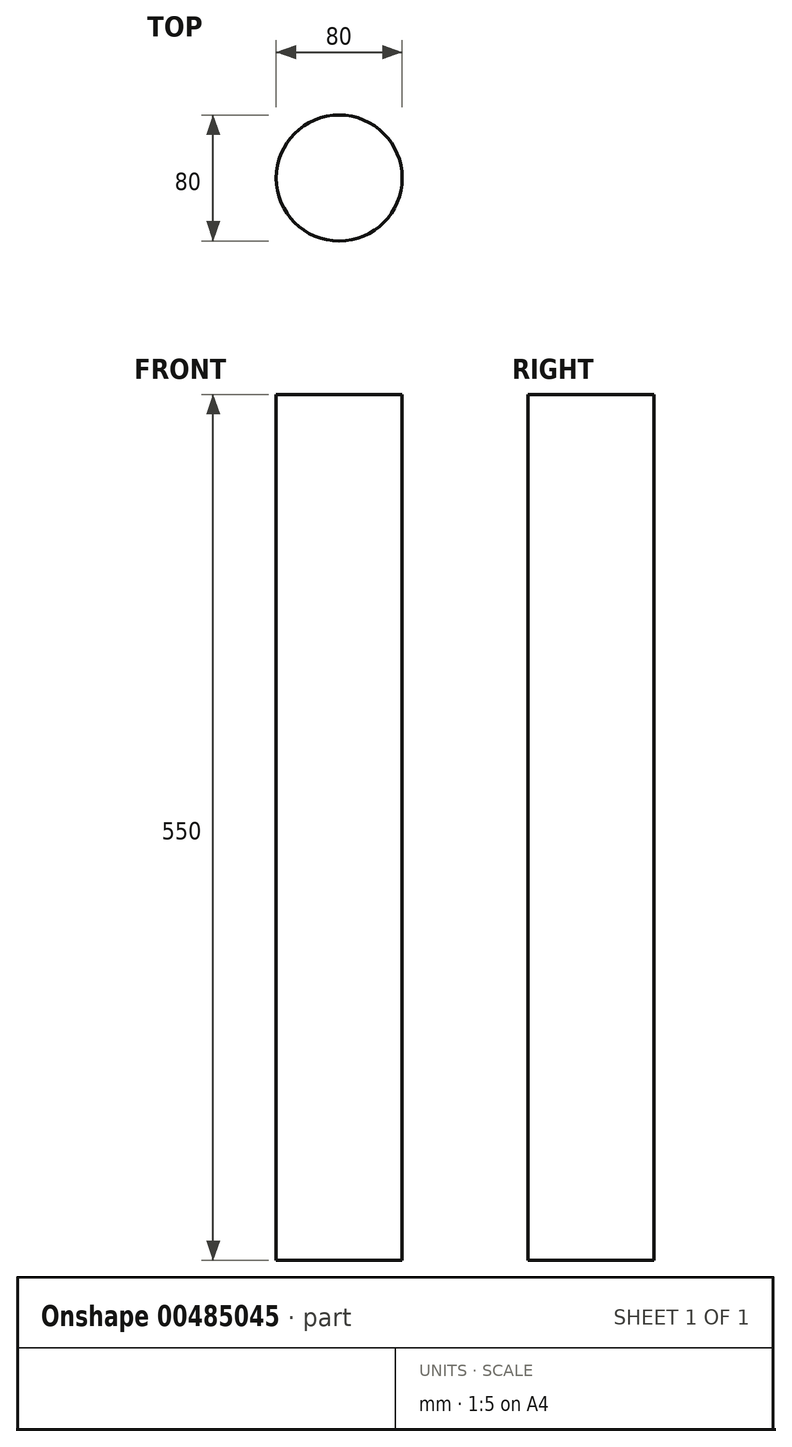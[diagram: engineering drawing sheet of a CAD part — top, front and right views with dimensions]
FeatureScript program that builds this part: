
annotation { "Feature Type Name" : "Feature", "Feature Type Description" : "" }
export const myFeature = defineFeature(function(context is Context, id is Id, definition is map)
    precondition{}
    {
        {
            var Q0;
            Q0=qCreatedBy(makeId("Top.planeOp"),FACE);
            var sketch = newSketch(context, id + "F0", { "sketchPlane" : qUnion([Q0])});
            skCircle(sketch, "E0", {"center": v(0, 0) * mm, "radius": 40 * mm});
            skSolve(sketch);
        }
        {
            var Q0;
            Q0=makeQuery(id+"F0.imprint","IMPRINT",FACE,{"disambiguationData":[TD([[makeQuery(id+"F0.imprint","IMPRINT",EDGE,{"derivedFrom":sQuery(id+"F0.wireOp",EDGE,"E0")}),1.0]])]});
            extrude(context, id + "F1", {"entities" : qUnion([Q0]), "depth" : 550 * mm});
        }
    });
